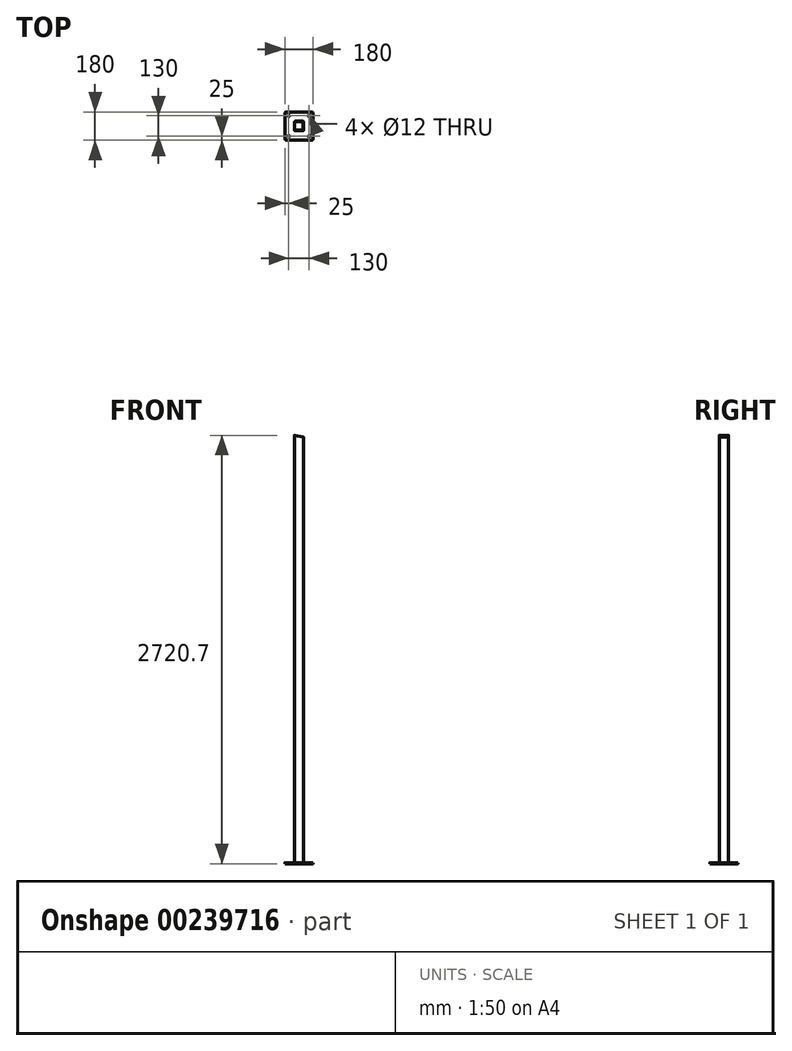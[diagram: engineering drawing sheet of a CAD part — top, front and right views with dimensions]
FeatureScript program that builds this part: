
annotation { "Feature Type Name" : "Feature", "Feature Type Description" : "" }
export const myFeature = defineFeature(function(context is Context, id is Id, definition is map)
    precondition{}
    {
        {
            var Q0;
            Q0=qCreatedBy(makeId("Top.planeOp"),FACE);
            var sketch = newSketch(context, id + "F0", { "sketchPlane" : qUnion([Q0])});
            skLineSegment(sketch, "E0.bottom", {"start": v(80, 90) * mm, "end": v(-80, 90) * mm});
            skLineSegment(sketch, "E0.top", {"start": v(80, -90) * mm, "end": v(-80, -90) * mm});
            skLineSegment(sketch, "E0.left", {"start": v(90, 80) * mm, "end": v(90, -80) * mm});
            skLineSegment(sketch, "E0.right", {"start": v(-90, 80) * mm, "end": v(-90, -80) * mm});
            skPoint(sketch, "E0.middle", {"position": v(0, 0) * mm});
            skPoint(sketch, "E1.visualSharp", {"position": v(-90, 90) * mm});
            skArc(sketch, "E1.filletArc", {"start": v(-80, 90) * mm, "mid": v(-87.07, 87.07) * mm, "end": v(-90, 80) * mm});
            skPoint(sketch, "E2.visualSharp", {"position": v(90, 90) * mm});
            skArc(sketch, "E2.filletArc", {"start": v(90, 80) * mm, "mid": v(87.07, 87.07) * mm, "end": v(80, 90) * mm});
            skPoint(sketch, "E3.visualSharp", {"position": v(90, -90) * mm});
            skArc(sketch, "E3.filletArc", {"start": v(80, -90) * mm, "mid": v(87.07, -87.07) * mm, "end": v(90, -80) * mm});
            skPoint(sketch, "E4.visualSharp", {"position": v(-90, -90) * mm});
            skArc(sketch, "E4.filletArc", {"start": v(-90, -80) * mm, "mid": v(-87.07, -87.07) * mm, "end": v(-80, -90) * mm});
            skCircle(sketch, "E5", {"center": v(-65, 65) * mm, "radius": 6 * mm});
            skCircle(sketch, "E6.0.1.0", {"center": v(-65, -65) * mm, "radius": 6 * mm});
            skCircle(sketch, "E6.1.0.0", {"center": v(65, 65) * mm, "radius": 6 * mm});
            skCircle(sketch, "E6.1.1.0", {"center": v(65, -65) * mm, "radius": 6 * mm});
            skLineSegment(sketch, "E6.direction1", {"start": v(-65, 65) * mm, "end": v(65, 65) * mm, "construction": true});
            skLineSegment(sketch, "E6.direction2", {"start": v(-65, 65) * mm, "end": v(-65, -65) * mm, "construction": true});
            skSolve(sketch);
        }
        {
            var Q0;
            Q0=makeQuery(id+"F0.imprint","IMPRINT",FACE,{"disambiguationData":[TD([[makeQuery(id+"F0.imprint","IMPRINT",EDGE,{"derivedFrom":sQuery(id+"F0.wireOp",EDGE,"E0.bottom")}),1.0]])]});
            extrude(context, id + "F1", {"entities" : qUnion([Q0]), "depth" : 6 * mm});
        }
        {
            var Q0;
            Q0=makeQuery(id+"F1.opExtrude","CAP_FACE",FACE,{"disambiguationData":[OSD([sQuery(id+"F0.wireOp",EDGE,"E0.bottom"),sQuery(id+"F0.wireOp",EDGE,"E0.top"),sQuery(id+"F0.wireOp",EDGE,"E0.left"),sQuery(id+"F0.wireOp",EDGE,"E0.right"),sQuery(id+"F0.wireOp",EDGE,"E1.filletArc"),sQuery(id+"F0.wireOp",EDGE,"E2.filletArc"),sQuery(id+"F0.wireOp",EDGE,"E3.filletArc"),sQuery(id+"F0.wireOp",EDGE,"E4.filletArc"),sQuery(id+"F0.wireOp",EDGE,"E5"),sQuery(id+"F0.wireOp",EDGE,"E6.0.1.0"),sQuery(id+"F0.wireOp",EDGE,"E6.1.0.0"),sQuery(id+"F0.wireOp",EDGE,"E6.1.1.0")])],"isStart":false});
            var sketch = newSketch(context, id + "F2", { "sketchPlane" : qUnion([Q0])});
            skLineSegment(sketch, "E7.bottom", {"start": v(25, -30) * mm, "end": v(-25, -30) * mm});
            skLineSegment(sketch, "E7.top", {"start": v(25, 30) * mm, "end": v(-25, 30) * mm});
            skLineSegment(sketch, "E7.left", {"start": v(30, -25) * mm, "end": v(30, 25) * mm});
            skLineSegment(sketch, "E7.right", {"start": v(-30, -25) * mm, "end": v(-30, 25) * mm});
            skPoint(sketch, "E7.middle", {"position": v(0, 0) * mm});
            skPoint(sketch, "E8.visualSharp", {"position": v(-30, 30) * mm});
            skArc(sketch, "E8.filletArc", {"start": v(-25, 30) * mm, "mid": v(-28.54, 28.54) * mm, "end": v(-30, 25) * mm});
            skPoint(sketch, "E9.visualSharp", {"position": v(30, 30) * mm});
            skArc(sketch, "E9.filletArc", {"start": v(30, 25) * mm, "mid": v(28.54, 28.54) * mm, "end": v(25, 30) * mm});
            skPoint(sketch, "E10.visualSharp", {"position": v(30, -30) * mm});
            skArc(sketch, "E10.filletArc", {"start": v(25, -30) * mm, "mid": v(28.54, -28.54) * mm, "end": v(30, -25) * mm});
            skPoint(sketch, "E11.visualSharp", {"position": v(-30, -30) * mm});
            skArc(sketch, "E11.filletArc", {"start": v(-30, -25) * mm, "mid": v(-28.54, -28.54) * mm, "end": v(-25, -30) * mm});
            skArc(sketch, "E12.0", {"start": v(27, 25) * mm, "mid": v(26.41, 26.41) * mm, "end": v(25, 27) * mm});
            skLineSegment(sketch, "E12.1", {"start": v(27, -25) * mm, "end": v(27, 25) * mm});
            skLineSegment(sketch, "E12.2", {"start": v(25, 27) * mm, "end": v(-25, 27) * mm});
            skArc(sketch, "E12.3", {"start": v(25, -27) * mm, "mid": v(26.41, -26.41) * mm, "end": v(27, -25) * mm});
            skArc(sketch, "E12.4", {"start": v(-25, 27) * mm, "mid": v(-26.41, 26.41) * mm, "end": v(-27, 25) * mm});
            skLineSegment(sketch, "E12.5", {"start": v(-27, -25) * mm, "end": v(-27, 25) * mm});
            skArc(sketch, "E12.6", {"start": v(-27, -25) * mm, "mid": v(-26.41, -26.41) * mm, "end": v(-25, -27) * mm});
            skLineSegment(sketch, "E12.7", {"start": v(25, -27) * mm, "end": v(-25, -27) * mm});
            skSolve(sketch);
        }
        {
            var Q0;
            Q0=makeQuery(id+"F2.imprint","IMPRINT",FACE,{"disambiguationData":[TD([[makeQuery(id+"F2.imprint","IMPRINT",EDGE,{"derivedFrom":sQuery(id+"F2.wireOp",EDGE,"E7.bottom")}),-1.0]])]});
            extrude(context, id + "F3", {"entities" : qUnion([Q0]), "operationType" : NewBodyOperationType.ADD, "depth" : 2714.7 * mm});
        }
        {
            var Q0;
            Q0=makeQuery(id+"F3.opExtrude","SWEPT_FACE",FACE,{"disambiguationData":[OSD([sQuery(id+"F2.wireOp",EDGE,"E7.bottom")])]});
            var sketch = newSketch(context, id + "F4", { "sketchPlane" : qUnion([Q0])});
            skLineSegment(sketch, "E13", {"start": v(-30.02, 2720.7) * mm, "end": v(31.37, 2720.7) * mm});
            skLineSegment(sketch, "E14", {"start": v(31.37, 2720.7) * mm, "end": v(31.37, 2709.87) * mm});
            skLineSegment(sketch, "E15", {"start": v(31.37, 2709.87) * mm, "end": v(-30.02, 2720.7) * mm});
            skSolve(sketch);
        }
        {
            var Q0;
            Q0=qSketchRegion(id+"F4",true);
            extrude(context, id + "F5", {"entities" : qUnion([Q0]), "operationType" : NewBodyOperationType.REMOVE, "endBound" : BoundingType.THROUGH_ALL, "oppositeDirection" : true, "depth" : 25 * mm});
        }
        {
            var Q0;
            {var subQ0=sQuery(id+"F0.wireOp",EDGE,"E6.0.1.0");var subQ1=sQuery(id+"F0.wireOp",EDGE,"E4.filletArc");var subQ2=sQuery(id+"F0.wireOp",EDGE,"E3.filletArc");var subQ3=sQuery(id+"F0.wireOp",EDGE,"E2.filletArc");var subQ4=sQuery(id+"F0.wireOp",EDGE,"E1.filletArc");var subQ5=sQuery(id+"F0.wireOp",EDGE,"E0.bottom");var subQ6=sQuery(id+"F0.wireOp",EDGE,"E5");var subQ7=sQuery(id+"F0.wireOp",EDGE,"E0.top");var subQ8=sQuery(id+"F0.wireOp",EDGE,"E0.left");var subQ9=sQuery(id+"F0.wireOp",EDGE,"E0.right");var subQ10=sQuery(id+"F0.wireOp",EDGE,"E6.1.0.0");var subQ11=sQuery(id+"F0.wireOp",EDGE,"E6.1.1.0");Q0=makeQuery(id+"F3.boolean.opBoolean","SPLIT",FACE,{"disambiguationData":[TD([makeQuery(id+"F1.opExtrude","SWEPT_FACE",FACE,{"disambiguationData":[OSD([subQ5])]})])],"derivedFrom":makeQuery(id+"F1.opExtrude","CAP_FACE",FACE,{"disambiguationData":[OSD([subQ5,subQ7,subQ8,subQ9,subQ4,subQ3,subQ2,subQ1,subQ6,subQ0,subQ10,subQ11])],"isStart":false})});}
            cPlane(context, id + "F6", {"entities" : qUnion([Q0]), "cplaneType" : CPlaneType.OFFSET, "offset" : 0 * mm, "width" : 150 * mm, "height" : 150 * mm});
        }
    });
